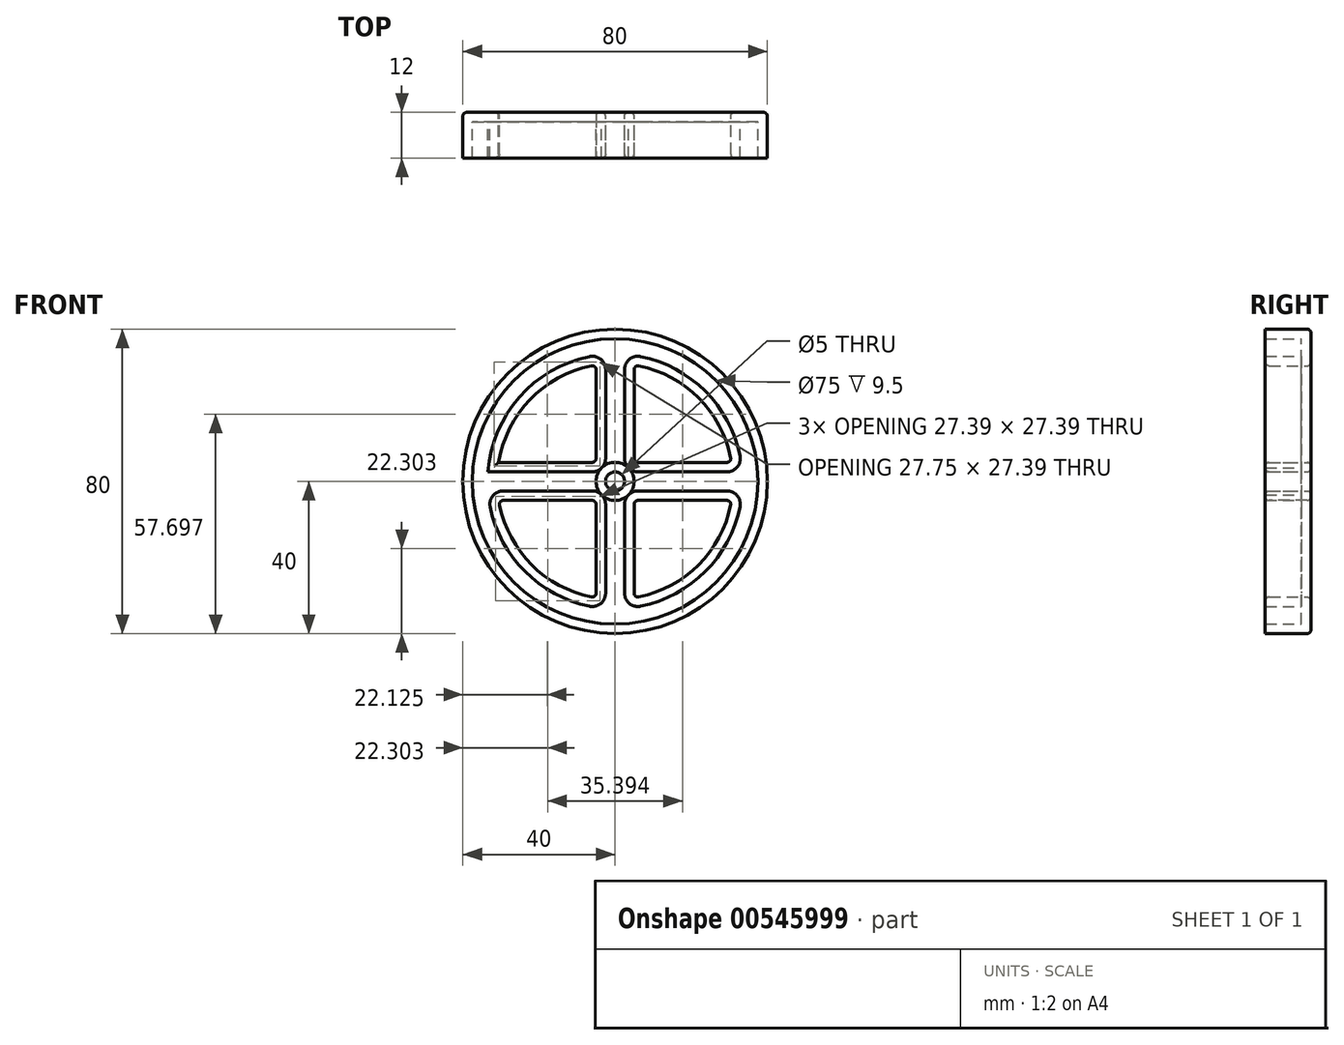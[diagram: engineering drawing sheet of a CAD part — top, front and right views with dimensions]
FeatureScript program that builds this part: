
annotation { "Feature Type Name" : "Feature", "Feature Type Description" : "" }
export const myFeature = defineFeature(function(context is Context, id is Id, definition is map)
    precondition{}
    {
        {
            var Q0;
            Q0=qCreatedBy(makeId("Front.planeOp"),FACE);
            var sketch = newSketch(context, id + "F0", { "sketchPlane" : qUnion([Q0])});
            skArc(sketch, "E0", {"start": v(-30.6, -5) * mm, "mid": v(-21.92, -21.92) * mm, "end": v(-5, -30.6) * mm});
            skCircle(sketch, "E1", {"center": v(0, 0) * mm, "radius": 40 * mm});
            skArc(sketch, "E2", {"start": v(5, -5.6) * mm, "mid": v(5.3, -5.3) * mm, "end": v(5.6, -5) * mm});
            skCircle(sketch, "E3", {"center": v(0, 0) * mm, "radius": 2.5 * mm});
            skLineSegment(sketch, "E4", {"start": v(0, 0) * mm, "end": v(0, 31) * mm, "construction": true});
            skLineSegment(sketch, "E5", {"start": v(0, 0) * mm, "end": v(31, 0) * mm, "construction": true});
            skLineSegment(sketch, "E6", {"start": v(0, 0) * mm, "end": v(0, -31) * mm, "construction": true});
            skLineSegment(sketch, "E7", {"start": v(0, 0) * mm, "end": v(-31, 0) * mm, "construction": true});
            skLineSegment(sketch, "E8.0", {"start": v(5, 5.6) * mm, "end": v(5, 30.6) * mm});
            skLineSegment(sketch, "E9.0", {"start": v(-5, 5.6) * mm, "end": v(-5, 30.6) * mm});
            skLineSegment(sketch, "E10.0", {"start": v(-5.6, 5) * mm, "end": v(-30.6, 5) * mm});
            skLineSegment(sketch, "E11.0", {"start": v(5.6, -5) * mm, "end": v(30.6, -5) * mm});
            skLineSegment(sketch, "E12.0", {"start": v(-5, -5.6) * mm, "end": v(-5, -30.6) * mm});
            skLineSegment(sketch, "E13.0", {"start": v(5, -5.6) * mm, "end": v(5, -30.6) * mm});
            skLineSegment(sketch, "E14.0", {"start": v(5.6, 5) * mm, "end": v(30.6, 5) * mm});
            skLineSegment(sketch, "E15.0", {"start": v(-5.6, -5) * mm, "end": v(-30.6, -5) * mm});
            skArc(sketch, "E16.trimOffspring", {"start": v(30.6, 5) * mm, "mid": v(21.92, 21.92) * mm, "end": v(5, 30.6) * mm});
            skArc(sketch, "E17.trimOffspring", {"start": v(-5, 30.6) * mm, "mid": v(-21.92, 21.92) * mm, "end": v(-30.6, 5) * mm});
            skArc(sketch, "E18.trimOffspring", {"start": v(5, -30.6) * mm, "mid": v(21.92, -21.92) * mm, "end": v(30.6, -5) * mm});
            skArc(sketch, "E19.trimOffspring", {"start": v(5.6, 5) * mm, "mid": v(5.3, 5.3) * mm, "end": v(5, 5.6) * mm});
            skArc(sketch, "E20.trimOffspring", {"start": v(-5, 5.6) * mm, "mid": v(-5.3, 5.3) * mm, "end": v(-5.6, 5) * mm});
            skArc(sketch, "E21.trimOffspring", {"start": v(-5.6, -5) * mm, "mid": v(-5.3, -5.3) * mm, "end": v(-5, -5.6) * mm});
            skSolve(sketch);
        }
        {
            var Q0;
            Q0=makeQuery(id+"F0.imprint","IMPRINT",FACE,{"disambiguationData":[TD([[makeQuery(id+"F0.imprint","IMPRINT",EDGE,{"derivedFrom":sQuery(id+"F0.wireOp",EDGE,"E0")}),-1.0]])]});
            var Q1;
            Q1=sQuery(id+"F0.wireOp",EDGE,"E0");
            var Q2;
            Q2=qCreatedBy(makeId("Front.planeOp"),FACE);
            extrude(context, id + "F1", {"entities" : qUnion([Q0]), "surfaceEntities" : qUnion([Q1]), "endBound" : BoundingType.SYMMETRIC, "depth" : 12 * mm, "endBoundEntityFace" : qUnion([Q2]), "offsetDistance" : 25 * mm});
        }
        {
            var Q0;
            Q0=makeQuery(id+"F1.opExtrude","CAP_EDGE",EDGE,{"disambiguationData":[OSD([sQuery(id+"F0.wireOp",EDGE,"E8.0")])],"isStart":false});
            var Q1;
            Q1=makeQuery(id+"F1.opExtrude","CAP_EDGE",EDGE,{"disambiguationData":[OSD([sQuery(id+"F0.wireOp",EDGE,"E14.0")])],"isStart":false});
            var Q2;
            Q2=makeQuery(id+"F1.opExtrude","CAP_EDGE",EDGE,{"disambiguationData":[OSD([sQuery(id+"F0.wireOp",EDGE,"E16.trimOffspring")])],"isStart":false});
            var Q3;
            Q3=makeQuery(id+"F1.opExtrude","SWEPT_EDGE",EDGE,{"disambiguationData":[OSD([sQuery(id+"F0.wireOp",EDGE,"E8.0"),sQuery(id+"F0.wireOp",EDGE,"E16.trimOffspring")])]});
            var Q4;
            Q4=makeQuery(id+"F1.opExtrude","CAP_EDGE",EDGE,{"disambiguationData":[OSD([sQuery(id+"F0.wireOp",EDGE,"E14.0")])],"isStart":true});
            var Q5;
            Q5=makeQuery(id+"F1.opExtrude","SWEPT_EDGE",EDGE,{"disambiguationData":[OSD([sQuery(id+"F0.wireOp",EDGE,"E14.0"),sQuery(id+"F0.wireOp",EDGE,"E16.trimOffspring")])]});
            var Q6;
            Q6=makeQuery(id+"F1.opExtrude","CAP_EDGE",EDGE,{"disambiguationData":[OSD([sQuery(id+"F0.wireOp",EDGE,"E16.trimOffspring")])],"isStart":true});
            var Q7;
            Q7=makeQuery(id+"F1.opExtrude","CAP_EDGE",EDGE,{"disambiguationData":[OSD([sQuery(id+"F0.wireOp",EDGE,"E10.0")])],"isStart":false});
            var Q8;
            Q8=makeQuery(id+"F1.opExtrude","SWEPT_EDGE",EDGE,{"disambiguationData":[OSD([sQuery(id+"F0.wireOp",EDGE,"E9.0"),sQuery(id+"F0.wireOp",EDGE,"E20.trimOffspring")])]});
            var Q9;
            Q9=makeQuery(id+"F1.opExtrude","CAP_EDGE",EDGE,{"disambiguationData":[OSD([sQuery(id+"F0.wireOp",EDGE,"E9.0")])],"isStart":false});
            var Q10;
            Q10=makeQuery(id+"F1.opExtrude","CAP_EDGE",EDGE,{"disambiguationData":[OSD([sQuery(id+"F0.wireOp",EDGE,"E10.0")])],"isStart":true});
            var Q11;
            Q11=makeQuery(id+"F1.opExtrude","CAP_EDGE",EDGE,{"disambiguationData":[OSD([sQuery(id+"F0.wireOp",EDGE,"E17.trimOffspring")])],"isStart":false});
            var Q12;
            Q12=makeQuery(id+"F1.opExtrude","SWEPT_EDGE",EDGE,{"disambiguationData":[OSD([sQuery(id+"F0.wireOp",EDGE,"E9.0"),sQuery(id+"F0.wireOp",EDGE,"E17.trimOffspring")])]});
            var Q13;
            Q13=makeQuery(id+"F1.opExtrude","CAP_EDGE",EDGE,{"disambiguationData":[OSD([sQuery(id+"F0.wireOp",EDGE,"E17.trimOffspring")])],"isStart":true});
            var Q14;
            Q14=makeQuery(id+"F1.opExtrude","SWEPT_EDGE",EDGE,{"disambiguationData":[OSD([sQuery(id+"F0.wireOp",EDGE,"E15.0"),sQuery(id+"F0.wireOp",EDGE,"E21.trimOffspring")])]});
            var Q15;
            Q15=makeQuery(id+"F1.opExtrude","SWEPT_EDGE",EDGE,{"disambiguationData":[OSD([sQuery(id+"F0.wireOp",EDGE,"E12.0"),sQuery(id+"F0.wireOp",EDGE,"E21.trimOffspring")])]});
            var Q16;
            Q16=makeQuery(id+"F1.opExtrude","CAP_EDGE",EDGE,{"disambiguationData":[OSD([sQuery(id+"F0.wireOp",EDGE,"E21.trimOffspring")])],"isStart":false});
            var Q17;
            Q17=makeQuery(id+"F1.opExtrude","CAP_EDGE",EDGE,{"disambiguationData":[OSD([sQuery(id+"F0.wireOp",EDGE,"E15.0")])],"isStart":false});
            var Q18;
            Q18=makeQuery(id+"F1.opExtrude","CAP_EDGE",EDGE,{"disambiguationData":[OSD([sQuery(id+"F0.wireOp",EDGE,"E12.0")])],"isStart":false});
            var Q19;
            Q19=makeQuery(id+"F1.opExtrude","CAP_EDGE",EDGE,{"disambiguationData":[OSD([sQuery(id+"F0.wireOp",EDGE,"E15.0")])],"isStart":true});
            var Q20;
            Q20=makeQuery(id+"F1.opExtrude","SWEPT_EDGE",EDGE,{"disambiguationData":[OSD([sQuery(id+"F0.wireOp",EDGE,"E0"),sQuery(id+"F0.wireOp",EDGE,"E15.0")])]});
            var Q21;
            Q21=makeQuery(id+"F1.opExtrude","CAP_EDGE",EDGE,{"disambiguationData":[OSD([sQuery(id+"F0.wireOp",EDGE,"E0")])],"isStart":false});
            var Q22;
            Q22=makeQuery(id+"F1.opExtrude","SWEPT_EDGE",EDGE,{"disambiguationData":[OSD([sQuery(id+"F0.wireOp",EDGE,"E0"),sQuery(id+"F0.wireOp",EDGE,"E12.0")])]});
            var Q23;
            Q23=makeQuery(id+"F1.opExtrude","CAP_EDGE",EDGE,{"disambiguationData":[OSD([sQuery(id+"F0.wireOp",EDGE,"E0")])],"isStart":true});
            var Q24;
            Q24=makeQuery(id+"F1.opExtrude","CAP_EDGE",EDGE,{"disambiguationData":[OSD([sQuery(id+"F0.wireOp",EDGE,"E12.0")])],"isStart":true});
            var Q25;
            Q25=makeQuery(id+"F1.opExtrude","SWEPT_EDGE",EDGE,{"disambiguationData":[OSD([sQuery(id+"F0.wireOp",EDGE,"E13.0"),sQuery(id+"F0.wireOp",EDGE,"E18.trimOffspring")])]});
            var Q26;
            Q26=makeQuery(id+"F1.opExtrude","SWEPT_EDGE",EDGE,{"disambiguationData":[OSD([sQuery(id+"F0.wireOp",EDGE,"E2"),sQuery(id+"F0.wireOp",EDGE,"E13.0")])]});
            var Q27;
            Q27=makeQuery(id+"F1.opExtrude","CAP_EDGE",EDGE,{"disambiguationData":[OSD([sQuery(id+"F0.wireOp",EDGE,"E2")])],"isStart":false});
            var Q28;
            Q28=makeQuery(id+"F1.opExtrude","CAP_EDGE",EDGE,{"disambiguationData":[OSD([sQuery(id+"F0.wireOp",EDGE,"E13.0")])],"isStart":false});
            var Q29;
            Q29=makeQuery(id+"F1.opExtrude","CAP_EDGE",EDGE,{"disambiguationData":[OSD([sQuery(id+"F0.wireOp",EDGE,"E11.0")])],"isStart":false});
            var Q30;
            Q30=makeQuery(id+"F1.opExtrude","SWEPT_EDGE",EDGE,{"disambiguationData":[OSD([sQuery(id+"F0.wireOp",EDGE,"E2"),sQuery(id+"F0.wireOp",EDGE,"E11.0")])]});
            var Q31;
            Q31=makeQuery(id+"F1.opExtrude","CAP_EDGE",EDGE,{"disambiguationData":[OSD([sQuery(id+"F0.wireOp",EDGE,"E18.trimOffspring")])],"isStart":false});
            var Q32;
            Q32=makeQuery(id+"F1.opExtrude","SWEPT_EDGE",EDGE,{"disambiguationData":[OSD([sQuery(id+"F0.wireOp",EDGE,"E11.0"),sQuery(id+"F0.wireOp",EDGE,"E18.trimOffspring")])]});
            var Q33;
            Q33=makeQuery(id+"F1.opExtrude","CAP_EDGE",EDGE,{"disambiguationData":[OSD([sQuery(id+"F0.wireOp",EDGE,"E11.0")])],"isStart":true});
            var Q34;
            Q34=makeQuery(id+"F1.opExtrude","CAP_EDGE",EDGE,{"disambiguationData":[OSD([sQuery(id+"F0.wireOp",EDGE,"E13.0")])],"isStart":true});
            var Q35;
            Q35=makeQuery(id+"F1.opExtrude","CAP_EDGE",EDGE,{"disambiguationData":[OSD([sQuery(id+"F0.wireOp",EDGE,"E20.trimOffspring")])],"isStart":true});
            var Q36;
            Q36=makeQuery(id+"F1.opExtrude","CAP_FACE",FACE,{"disambiguationData":[OSD([sQuery(id+"F0.wireOp",EDGE,"E0"),sQuery(id+"F0.wireOp",EDGE,"E1"),sQuery(id+"F0.wireOp",EDGE,"E2"),sQuery(id+"F0.wireOp",EDGE,"E3"),sQuery(id+"F0.wireOp",EDGE,"E8.0"),sQuery(id+"F0.wireOp",EDGE,"E9.0"),sQuery(id+"F0.wireOp",EDGE,"E10.0"),sQuery(id+"F0.wireOp",EDGE,"E11.0"),sQuery(id+"F0.wireOp",EDGE,"E12.0"),sQuery(id+"F0.wireOp",EDGE,"E13.0"),sQuery(id+"F0.wireOp",EDGE,"E14.0"),sQuery(id+"F0.wireOp",EDGE,"E15.0"),sQuery(id+"F0.wireOp",EDGE,"E16.trimOffspring"),sQuery(id+"F0.wireOp",EDGE,"E17.trimOffspring"),sQuery(id+"F0.wireOp",EDGE,"E18.trimOffspring"),sQuery(id+"F0.wireOp",EDGE,"E19.trimOffspring"),sQuery(id+"F0.wireOp",EDGE,"E20.trimOffspring"),sQuery(id+"F0.wireOp",EDGE,"E21.trimOffspring")])],"isStart":true});
            var Q37;
            Q37=makeQuery(id+"F1.opExtrude","CAP_EDGE",EDGE,{"disambiguationData":[OSD([sQuery(id+"F0.wireOp",EDGE,"E8.0")])],"isStart":true});
            var Q38;
            Q38=makeQuery(id+"F1.opExtrude","CAP_EDGE",EDGE,{"disambiguationData":[OSD([sQuery(id+"F0.wireOp",EDGE,"E9.0")])],"isStart":true});
            var Q39;
            Q39=makeQuery(id+"F1.opExtrude","CAP_EDGE",EDGE,{"disambiguationData":[OSD([sQuery(id+"F0.wireOp",EDGE,"E20.trimOffspring")])],"isStart":false});
            var Q40;
            Q40=makeQuery(id+"F1.opExtrude","SWEPT_EDGE",EDGE,{"disambiguationData":[OSD([sQuery(id+"F0.wireOp",EDGE,"E10.0"),sQuery(id+"F0.wireOp",EDGE,"E20.trimOffspring")])]});
            var Q41;
            Q41=makeQuery(id+"F1.opExtrude","SWEPT_EDGE",EDGE,{"disambiguationData":[OSD([sQuery(id+"F0.wireOp",EDGE,"E8.0"),sQuery(id+"F0.wireOp",EDGE,"E19.trimOffspring")])]});
            var Q42;
            Q42=makeQuery(id+"F1.opExtrude","SWEPT_EDGE",EDGE,{"disambiguationData":[OSD([sQuery(id+"F0.wireOp",EDGE,"E14.0"),sQuery(id+"F0.wireOp",EDGE,"E19.trimOffspring")])]});
            var Q43;
            Q43=makeQuery(id+"F1.opExtrude","CAP_EDGE",EDGE,{"disambiguationData":[OSD([sQuery(id+"F0.wireOp",EDGE,"E19.trimOffspring")])],"isStart":true});
            var Q44;
            Q44=makeQuery(id+"F1.opExtrude","CAP_EDGE",EDGE,{"disambiguationData":[OSD([sQuery(id+"F0.wireOp",EDGE,"E19.trimOffspring")])],"isStart":false});
            var Q45;
            Q45=makeQuery(id+"F1.opExtrude","CAP_EDGE",EDGE,{"disambiguationData":[OSD([sQuery(id+"F0.wireOp",EDGE,"E3")])],"isStart":false});
            var Q46;
            Q46=makeQuery(id+"F1.opExtrude","CAP_EDGE",EDGE,{"disambiguationData":[OSD([sQuery(id+"F0.wireOp",EDGE,"E3")])],"isStart":true});
            fillet(context, id + "F2", {"entities" : qUnion([Q0, Q1, Q2, Q3, Q4, Q5, Q6, Q7, Q8, Q9, Q10, Q11, Q12, Q13, Q14, Q15, Q16, Q17, Q18, Q19, Q20, Q21, Q22, Q23, Q24, Q25, Q26, Q27, Q28, Q29, Q30, Q31, Q32, Q33, Q34, Q35, Q36, Q37, Q38, Q39, Q40, Q41, Q42, Q43, Q44, Q45, Q46]), "radius" : 1 * mm, "tangentPropagation" : true, "allowEdgeOverflow" : false});
        }
        {
            var Q0;
            Q0=makeQuery(id+"F1.opExtrude","CAP_FACE",FACE,{"disambiguationData":[OSD([sQuery(id+"F0.wireOp",EDGE,"E0"),sQuery(id+"F0.wireOp",EDGE,"E1"),sQuery(id+"F0.wireOp",EDGE,"E2"),sQuery(id+"F0.wireOp",EDGE,"E3"),sQuery(id+"F0.wireOp",EDGE,"E8.0"),sQuery(id+"F0.wireOp",EDGE,"E9.0"),sQuery(id+"F0.wireOp",EDGE,"E10.0"),sQuery(id+"F0.wireOp",EDGE,"E11.0"),sQuery(id+"F0.wireOp",EDGE,"E12.0"),sQuery(id+"F0.wireOp",EDGE,"E13.0"),sQuery(id+"F0.wireOp",EDGE,"E14.0"),sQuery(id+"F0.wireOp",EDGE,"E15.0"),sQuery(id+"F0.wireOp",EDGE,"E16.trimOffspring"),sQuery(id+"F0.wireOp",EDGE,"E17.trimOffspring"),sQuery(id+"F0.wireOp",EDGE,"E18.trimOffspring"),sQuery(id+"F0.wireOp",EDGE,"E19.trimOffspring"),sQuery(id+"F0.wireOp",EDGE,"E20.trimOffspring"),sQuery(id+"F0.wireOp",EDGE,"E21.trimOffspring")])],"isStart":false});
            shell(context, id + "F3", {"entities" : qUnion([Q0]), "thickness" : 2.5 * mm});
        }
    });
